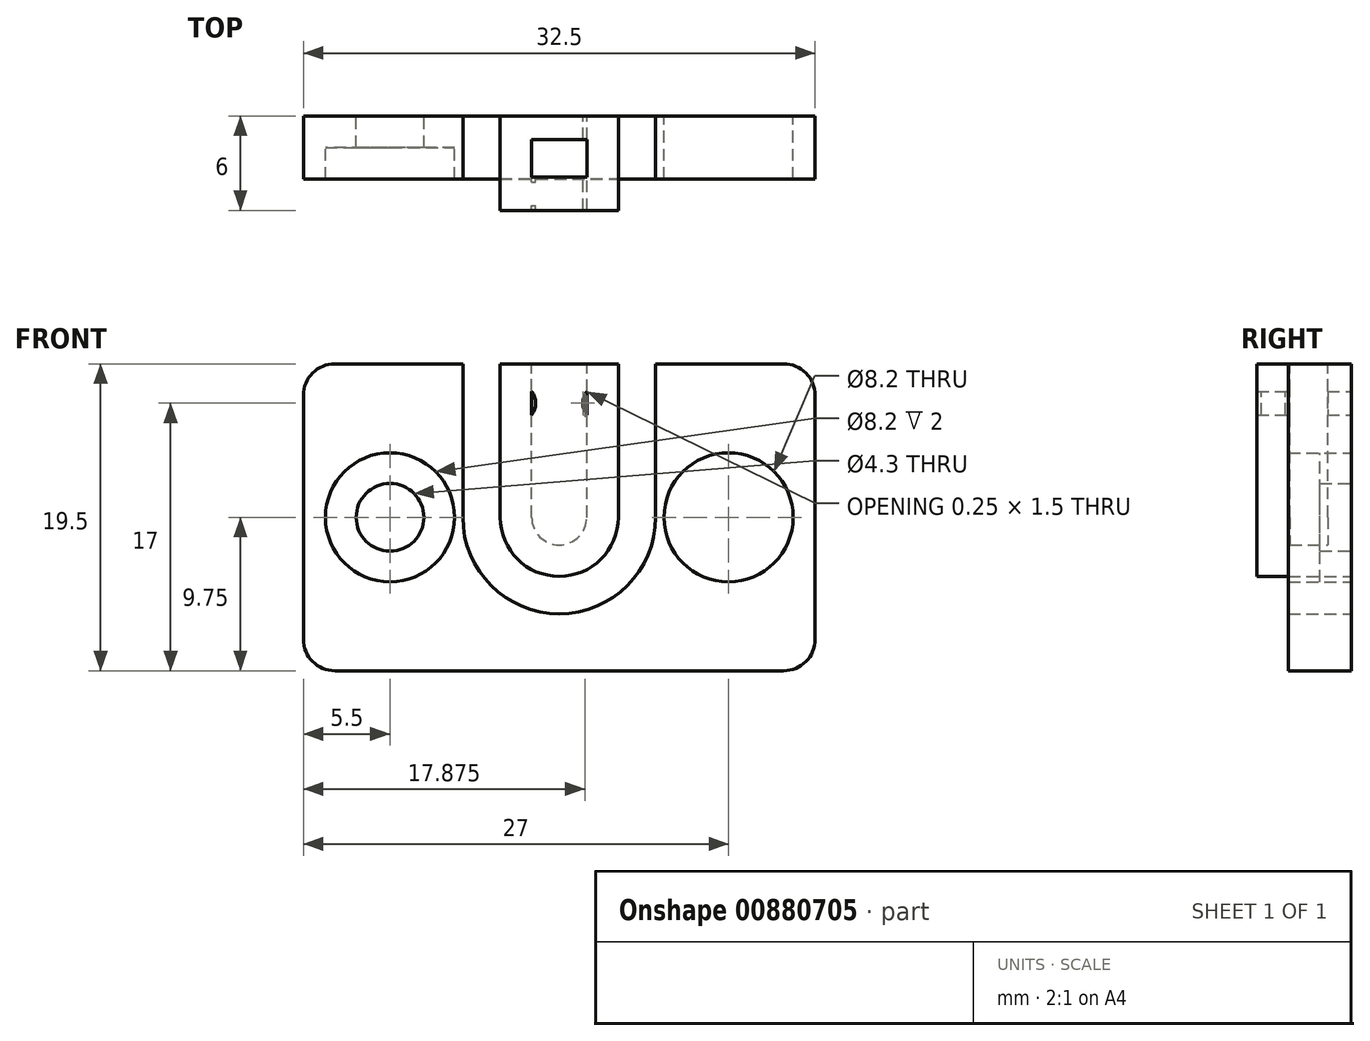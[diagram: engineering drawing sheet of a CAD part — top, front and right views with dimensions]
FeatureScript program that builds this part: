
annotation { "Feature Type Name" : "Feature", "Feature Type Description" : "" }
export const myFeature = defineFeature(function(context is Context, id is Id, definition is map)
    precondition{}
    {
        {
            var Q0;
            Q0=qCreatedBy(makeId("Front.planeOp"),FACE);
            var sketch = newSketch(context, id + "F0", { "sketchPlane" : qUnion([Q0])});
            skArc(sketch, "E0", {"start": v(1.75, 0) * mm, "mid": v(0, -1.75) * mm, "end": v(-1.75, 0) * mm});
            skArc(sketch, "E1", {"start": v(3.75, 0) * mm, "mid": v(0, -3.75) * mm, "end": v(-3.75, 0) * mm});
            skLineSegment(sketch, "E2.bottom", {"start": v(14.25, 9.75) * mm, "end": v(-14.25, 9.75) * mm});
            skLineSegment(sketch, "E2.top", {"start": v(14.25, -9.75) * mm, "end": v(-14.25, -9.75) * mm});
            skLineSegment(sketch, "E2.left", {"start": v(16.25, 7.75) * mm, "end": v(16.25, -7.75) * mm});
            skLineSegment(sketch, "E2.right", {"start": v(-16.25, 7.75) * mm, "end": v(-16.25, -7.75) * mm});
            skLineSegment(sketch, "E3", {"start": v(-1.75, 0) * mm, "end": v(-1.75, 9.75) * mm});
            skLineSegment(sketch, "E4", {"start": v(1.75, 0) * mm, "end": v(1.75, 9.75) * mm});
            skLineSegment(sketch, "E5", {"start": v(-3.75, 0) * mm, "end": v(-3.75, 9.75) * mm});
            skLineSegment(sketch, "E6", {"start": v(3.75, 0) * mm, "end": v(3.75, 9.75) * mm});
            skLineSegment(sketch, "E7.0", {"start": v(-6.12, 0) * mm, "end": v(-6.12, 9.75) * mm});
            skArc(sketch, "E7.1", {"start": v(6.13, 0) * mm, "mid": v(0, -6.13) * mm, "end": v(-6.13, 0) * mm});
            skLineSegment(sketch, "E7.2", {"start": v(6.13, 0) * mm, "end": v(6.13, 9.75) * mm});
            skCircle(sketch, "E8", {"center": v(-10.75, 0) * mm, "radius": 2.15 * mm});
            skCircle(sketch, "E9", {"center": v(-10.75, 0) * mm, "radius": 4.1 * mm});
            skLineSegment(sketch, "E10", {"start": v(0, 0) * mm, "end": v(0, 9.75) * mm, "construction": true});
            skCircle(sketch, "E11.MirrorC", {"center": v(10.75, 0) * mm, "radius": 4.1 * mm});
            skCircle(sketch, "E12.MirrorC", {"center": v(10.75, 0) * mm, "radius": 2.15 * mm});
            skArc(sketch, "E13", {"start": v(-1.75, 6.5) * mm, "mid": v(-1.5, 7.25) * mm, "end": v(-1.75, 8) * mm});
            skArc(sketch, "E14.MirrorCS", {"start": v(1.75, 6.5) * mm, "mid": v(1.5, 7.25) * mm, "end": v(1.75, 8) * mm});
            skPoint(sketch, "E15.visualSharp", {"position": v(-16.25, 9.75) * mm});
            skArc(sketch, "E15.filletArc", {"start": v(-14.25, 9.75) * mm, "mid": v(-15.66, 9.16) * mm, "end": v(-16.25, 7.75) * mm});
            skPoint(sketch, "E16.visualSharp", {"position": v(16.25, 9.75) * mm});
            skArc(sketch, "E16.filletArc", {"start": v(16.25, 7.75) * mm, "mid": v(15.66, 9.16) * mm, "end": v(14.25, 9.75) * mm});
            skPoint(sketch, "E17.visualSharp", {"position": v(16.25, -9.75) * mm});
            skArc(sketch, "E17.filletArc", {"start": v(14.25, -9.75) * mm, "mid": v(15.66, -9.16) * mm, "end": v(16.25, -7.75) * mm});
            skPoint(sketch, "E18.visualSharp", {"position": v(-16.25, -9.75) * mm});
            skArc(sketch, "E18.filletArc", {"start": v(-16.25, -7.75) * mm, "mid": v(-15.66, -9.16) * mm, "end": v(-14.25, -9.75) * mm});
            skSolve(sketch);
        }
        {
            var Q0;
            Q0=makeQuery(id+"F0.imprint","IMPRINT",FACE,{"disambiguationData":[TD([[makeQuery(id+"F0.imprint","IMPRINT",EDGE,{"derivedFrom":sQuery(id+"F0.wireOp",EDGE,"E2.top")}),-1.0]])]});
            var Q1;
            Q1=makeQuery(id+"F0.imprint","IMPRINT",FACE,{"disambiguationData":[TD([[makeQuery(id+"F0.imprint","IMPRINT",EDGE,{"derivedFrom":sQuery(id+"F0.wireOp",EDGE,"E1")}),1.0]])]});
            extrude(context, id + "F1", {"entities" : qUnion([Q0, Q1]), "depth" : 4 * mm, "offsetDistance" : 25 * mm});
        }
        {
            var Q0;
            {var subQ0=sQuery(id+"F0.wireOp",EDGE,"E14.MirrorCS");Q0=makeQuery(id+"F0.imprint","IMPRINT",FACE,{"disambiguationData":[TD([[makeQuery(id+"F0.imprint","IMPRINT",EDGE,{"derivedFrom":subQ0}),-1.0]])]});}
            var Q1;
            {var subQ10=sQuery(id+"F0.wireOp",EDGE,"E0");Q1=makeQuery(id+"F0.imprint","IMPRINT",FACE,{"disambiguationData":[TD([[makeQuery(id+"F0.imprint","IMPRINT",EDGE,{"derivedFrom":subQ10}),1.0]])]});}
            var Q2;
            {var subQ0=sQuery(id+"F0.wireOp",EDGE,"E13");Q2=makeQuery(id+"F0.imprint","IMPRINT",FACE,{"disambiguationData":[TD([[makeQuery(id+"F0.imprint","IMPRINT",EDGE,{"derivedFrom":subQ0}),1.0]])]});}
            var Q3;
            {var subQ4=sQuery(id+"F0.wireOp",EDGE,"E0");Q3=makeQuery(id+"F0.imprint","IMPRINT",FACE,{"disambiguationData":[TD([[makeQuery(id+"F0.imprint","IMPRINT",EDGE,{"derivedFrom":subQ4}),-1.0]])]});}
            extrude(context, id + "F2", {"entities" : qUnion([Q0, Q1, Q2, Q3]), "operationType" : NewBodyOperationType.ADD, "depth" : 1.5 * mm, "offsetDistance" : 25 * mm});
        }
        {
            var Q0;
            Q0=makeQuery(id+"F0.imprint","IMPRINT",FACE,{"disambiguationData":[TD([[makeQuery(id+"F0.imprint","IMPRINT",EDGE,{"derivedFrom":sQuery(id+"F0.wireOp",EDGE,"E1")}),1.0]])]});
            extrude(context, id + "F3", {"entities" : qUnion([Q0]), "operationType" : NewBodyOperationType.ADD, "depth" : 6 * mm, "offsetDistance" : 25 * mm});
        }
        {
            var Q0;
            Q0=makeQuery(id+"F0.imprint","IMPRINT",FACE,{"disambiguationData":[TD([[makeQuery(id+"F0.imprint","IMPRINT",EDGE,{"derivedFrom":sQuery(id+"F0.wireOp",EDGE,"E8")}),-1.0]])]});
            var Q1;
            Q1=makeQuery(id+"F0.imprint","IMPRINT",FACE,{"disambiguationData":[TD([[makeQuery(id+"F0.imprint","IMPRINT",EDGE,{"derivedFrom":sQuery(id+"F0.wireOp",EDGE,"E11.MirrorC")}),-1.0]])]});
            extrude(context, id + "F4", {"entities" : qUnion([Q0, Q1]), "operationType" : NewBodyOperationType.ADD, "depth" : 2 * mm, "offsetDistance" : 25 * mm});
        }
        {
            var Q0;
            {var subQ10=sQuery(id+"F0.wireOp",EDGE,"E0");Q0=makeQuery(id+"F0.imprint","IMPRINT",FACE,{"disambiguationData":[TD([[makeQuery(id+"F0.imprint","IMPRINT",EDGE,{"derivedFrom":subQ10}),1.0]])]});}
            var Q1;
            Q1=makeQuery(id+"F3.opExtrude","CAP_FACE",FACE,{"disambiguationData":[OSD([sQuery(id+"F0.wireOp",EDGE,"E1"),sQuery(id+"F0.wireOp",EDGE,"E2.bottom"),sQuery(id+"F0.wireOp",EDGE,"E5"),sQuery(id+"F0.wireOp",EDGE,"E6"),sQuery(id+"F0.wireOp",EDGE,"E7.0"),sQuery(id+"F0.wireOp",EDGE,"E7.1"),sQuery(id+"F0.wireOp",EDGE,"E7.2")])],"isStart":false});
            extrude(context, id + "F5", {"entities" : qUnion([Q0]), "operationType" : NewBodyOperationType.ADD, "endBound" : BoundingType.UP_TO_SURFACE, "depth" : 25 * mm, "endBoundEntityFace" : qUnion([Q1]), "offsetDistance" : 25 * mm, "hasSecondDirection" : true, "secondDirectionOppositeDirection" : false, "secondDirectionDepth" : 3.9 * mm});
        }
        {
            var Q0;
            {var subQ0=sQuery(id+"F0.wireOp",EDGE,"E13");Q0=makeQuery(id+"F0.imprint","IMPRINT",FACE,{"disambiguationData":[TD([[makeQuery(id+"F0.imprint","IMPRINT",EDGE,{"derivedFrom":subQ0}),1.0]])]});}
            var Q1;
            {var subQ0=sQuery(id+"F0.wireOp",EDGE,"E14.MirrorCS");Q1=makeQuery(id+"F0.imprint","IMPRINT",FACE,{"disambiguationData":[TD([[makeQuery(id+"F0.imprint","IMPRINT",EDGE,{"derivedFrom":subQ0}),-1.0]])]});}
            extrude(context, id + "F6", {"entities" : qUnion([Q0, Q1]), "operationType" : NewBodyOperationType.ADD, "depth" : 5.7 * mm, "offsetDistance" : 25 * mm, "hasSecondDirection" : true, "secondDirectionOppositeDirection" : false, "secondDirectionDepth" : 4.2 * mm});
        }
    });
